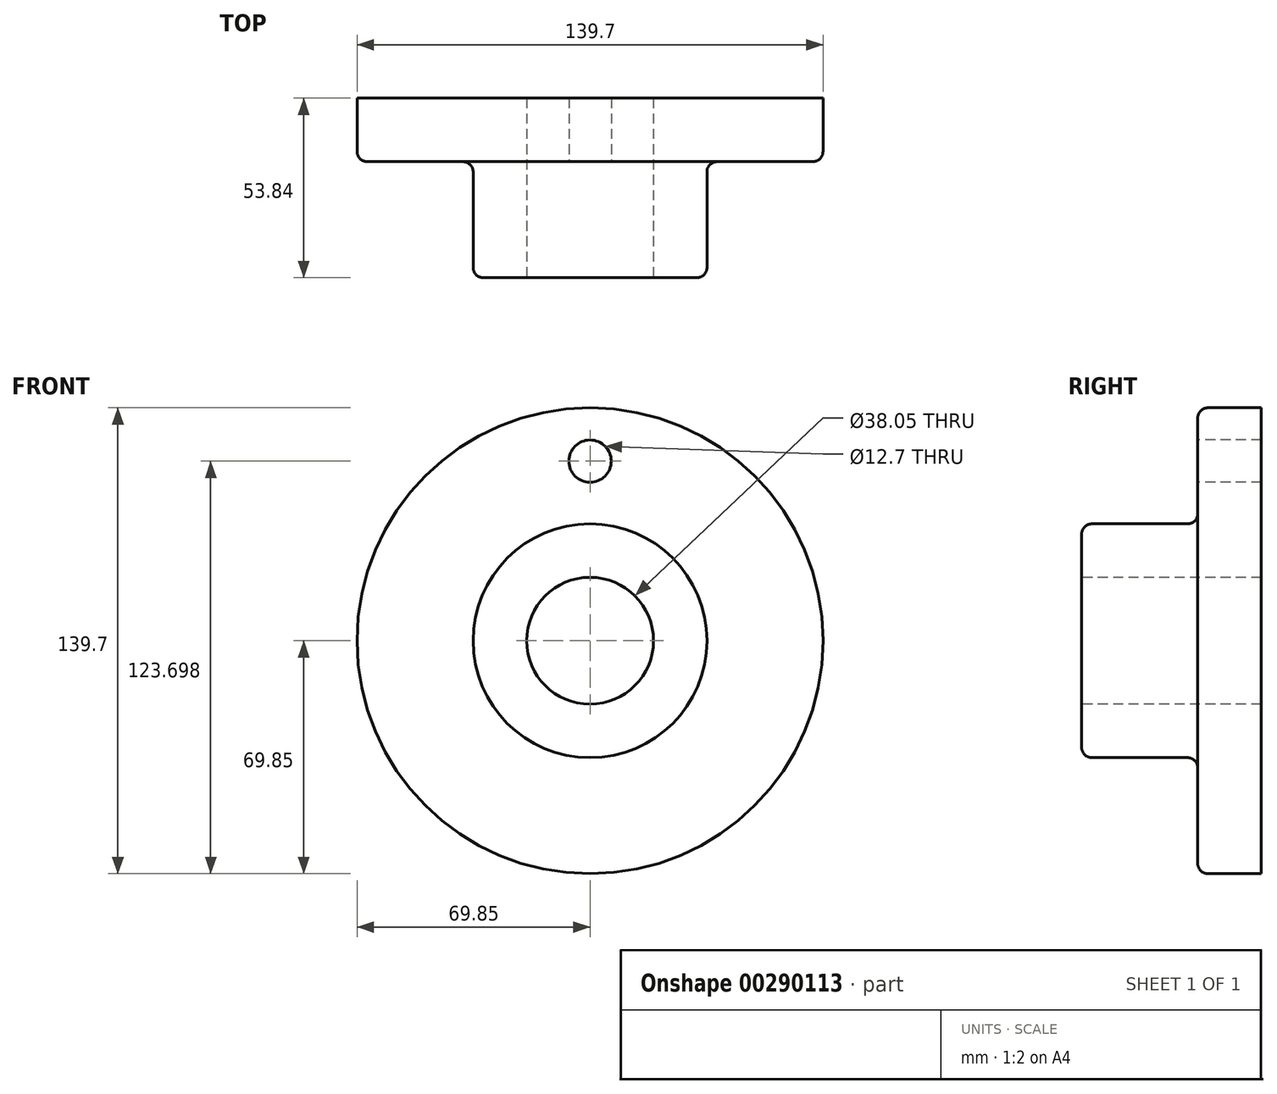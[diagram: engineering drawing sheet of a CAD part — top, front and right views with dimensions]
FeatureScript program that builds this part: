
annotation { "Feature Type Name" : "Feature", "Feature Type Description" : "" }
export const myFeature = defineFeature(function(context is Context, id is Id, definition is map)
    precondition{}
    {
        {
            var Q0;
            Q0=qCreatedBy(makeId("Right.planeOp"),FACE);
            var sketch = newSketch(context, id + "F0", { "sketchPlane" : qUnion([Q0])});
            skLineSegment(sketch, "E0", {"start": v(-26.92, 0) * mm, "end": v(26.92, 0) * mm, "construction": true});
            skLineSegment(sketch, "E1", {"start": v(-26.92, 19.02) * mm, "end": v(26.92, 19.02) * mm});
            skLineSegment(sketch, "E2", {"start": v(26.92, 19.02) * mm, "end": v(26.92, 69.85) * mm});
            skLineSegment(sketch, "E3", {"start": v(26.92, 69.85) * mm, "end": v(7.87, 69.85) * mm});
            skLineSegment(sketch, "E4", {"start": v(7.87, 69.85) * mm, "end": v(7.87, 35.05) * mm});
            skLineSegment(sketch, "E5", {"start": v(7.87, 35.05) * mm, "end": v(-26.92, 35.05) * mm});
            skLineSegment(sketch, "E6", {"start": v(-26.92, 35.05) * mm, "end": v(-26.92, 19.02) * mm});
            skPoint(sketch, "E7", {"position": v(0, 19.02) * mm});
            skSolve(sketch);
        }
        {
            var Q0;
            Q0=makeQuery(id+"F0.imprint","IMPRINT",FACE,{"disambiguationData":[TD([[makeQuery(id+"F0.imprint","IMPRINT",EDGE,{"derivedFrom":sQuery(id+"F0.wireOp",EDGE,"E1")}),1.0]])]});
            var Q1;
            Q1=sQuery(id+"F0.wireOp",EDGE,"E0");
            revolve(context, id + "F1", {"entities" : qUnion([Q0]), "axis" : qUnion([Q1]), "revolveType" : RevolveType.FULL});
        }
        {
            var Q0;
            Q0=makeQuery(id+"F1.opRevolve","SWEPT_EDGE",EDGE,{"disambiguationData":[OSD([sQuery(id+"F0.wireOp",EDGE,"E5"),sQuery(id+"F0.wireOp",EDGE,"E6")])]});
            var Q1;
            Q1=makeQuery(id+"F1.opRevolve","SWEPT_EDGE",EDGE,{"disambiguationData":[OSD([sQuery(id+"F0.wireOp",EDGE,"E3"),sQuery(id+"F0.wireOp",EDGE,"E4")])]});
            var Q2;
            Q2=makeQuery(id+"F1.opRevolve","SWEPT_EDGE",EDGE,{"disambiguationData":[OSD([sQuery(id+"F0.wireOp",EDGE,"E4"),sQuery(id+"F0.wireOp",EDGE,"E5")])]});
            fillet(context, id + "F2", {"entities" : qUnion([Q0, Q1, Q2]), "radius" : 3.05 * mm, "tangentPropagation" : true, "allowEdgeOverflow" : false});
        }
        {
            var Q0;
            Q0=makeQuery(id+"F1.opRevolve","SWEPT_FACE",FACE,{"disambiguationData":[OSD([sQuery(id+"F0.wireOp",EDGE,"E4")])]});
            var sketch = newSketch(context, id + "F3", { "sketchPlane" : qUnion([Q0])});
            skCircle(sketch, "E8", {"center": v(0, 53.85) * mm, "radius": 6.35 * mm});
            skSolve(sketch);
        }
        {
            var Q0;
            Q0=makeQuery(id+"F3.imprint","IMPRINT",FACE,{"disambiguationData":[TD([[makeQuery(id+"F3.imprint","IMPRINT",EDGE,{"derivedFrom":sQuery(id+"F3.wireOp",EDGE,"E8")}),1.0]])]});
            extrude(context, id + "F4", {"entities" : qUnion([Q0]), "operationType" : NewBodyOperationType.REMOVE, "endBound" : BoundingType.THROUGH_ALL, "oppositeDirection" : true, "depth" : 25.4 * mm});
        }
    });
